annotation { "Feature Type Name" : "Feature", "Feature Type Description" : "" }
export const myFeature = defineFeature(function(context is Context, id is Id, definition is map)
    precondition{}
    {
        {
            var Q0;
            Q0=qCreatedBy(makeId("Top.planeOp"),FACE);
            var sketch = newSketch(context, id + "F0", { "sketchPlane" : qUnion([Q0])});
            skLineSegment(sketch, "E0.bottom", {"start": v(-2.5, 54.86) * mm, "end": v(-0.5, 54.86) * mm});
            skLineSegment(sketch, "E0.right", {"start": v(-0.5, 54.86) * mm, "end": v(-0.5, 51.86) * mm});
            skLineSegment(sketch, "E1", {"start": v(-5.5, 18.86) * mm, "end": v(-2.5, 54.86) * mm});
            skLineSegment(sketch, "E2", {"start": v(-5.5, 18.86) * mm, "end": v(-26.33, -16.13) * mm});
            skLineSegment(sketch, "E3", {"start": v(-0.5, 18.86) * mm, "end": v(-2.64, 6.75) * mm});
            skLineSegment(sketch, "E4", {"start": v(-12.15, -20.66) * mm, "end": v(-23.75, -20.66) * mm});
            skPoint(sketch, "E5.visualSharp", {"position": v(-29.03, -20.66) * mm});
            skArc(sketch, "E5.filletArc", {"start": v(-26.33, -16.13) * mm, "mid": v(-26.36, -19.15) * mm, "end": v(-23.75, -20.66) * mm});
            skPoint(sketch, "E6.visualSharp", {"position": v(-7.47, -20.66) * mm});
            skLineSegment(sketch, "E7", {"start": v(-6.12, -13.03) * mm, "end": v(-7.03, -18.18) * mm});
            skLineSegment(sketch, "E8", {"start": v(-9.99, -20.66) * mm, "end": v(-12.15, -20.66) * mm});
            skArc(sketch, "E9.filletArc", {"start": v(-9.99, -20.66) * mm, "mid": v(-8.06, -19.96) * mm, "end": v(-7.03, -18.18) * mm});
            skLineSegment(sketch, "E10.0", {"start": v(-6.02, 13.1) * mm, "end": v(-24.63, -18.16) * mm});
            skLineSegment(sketch, "E10.1", {"start": v(-12.15, -18.16) * mm, "end": v(-24.63, -18.16) * mm});
            skLineSegment(sketch, "E10.2", {"start": v(-4.17, 12.42) * mm, "end": v(-8.59, -12.6) * mm});
            skLineSegment(sketch, "E10.3", {"start": v(-8.59, -12.6) * mm, "end": v(-9.57, -18.16) * mm});
            skLineSegment(sketch, "E10.4", {"start": v(-9.57, -18.16) * mm, "end": v(-12.15, -18.16) * mm});
            skPoint(sketch, "E11.visualSharp", {"position": v(-3.23, 17.8) * mm});
            skArc(sketch, "E11.filletArc", {"start": v(-4.17, 12.42) * mm, "mid": v(-4.81, 13.53) * mm, "end": v(-6.02, 13.1) * mm});
            skArc(sketch, "E12", {"start": v(-1.44, 8.44) * mm, "mid": v(-2.1, 7.64) * mm, "end": v(-2.64, 6.75) * mm});
            skArc(sketch, "E13", {"start": v(-1.18, 6.39) * mm, "mid": v(-2.23, 5.44) * mm, "end": v(-3.07, 4.29) * mm});
            skLineSegment(sketch, "E14.trimOffspring", {"start": v(-3.07, 4.29) * mm, "end": v(-6.12, -13.03) * mm});
            skArc(sketch, "E15.MirrorCS", {"start": v(9.99, -20.66) * mm, "mid": v(8.06, -19.96) * mm, "end": v(7.03, -18.18) * mm});
            skLineSegment(sketch, "E16.MirrorCS", {"start": v(9.99, -20.66) * mm, "end": v(12.15, -20.66) * mm});
            skLineSegment(sketch, "E17.MirrorCS", {"start": v(9.57, -18.16) * mm, "end": v(12.15, -18.16) * mm});
            skArc(sketch, "E18.MirrorCS", {"start": v(4.17, 12.42) * mm, "mid": v(4.81, 13.53) * mm, "end": v(6.02, 13.1) * mm});
            skArc(sketch, "E19.MirrorCS", {"start": v(26.33, -16.13) * mm, "mid": v(26.36, -19.15) * mm, "end": v(23.75, -20.66) * mm});
            skArc(sketch, "E20.MirrorCS", {"start": v(1.44, 8.44) * mm, "mid": v(2.1, 7.64) * mm, "end": v(2.64, 6.75) * mm});
            skLineSegment(sketch, "E21.MirrorCS", {"start": v(0.5, 18.86) * mm, "end": v(2.64, 6.75) * mm});
            skLineSegment(sketch, "E22.MirrorCS", {"start": v(6.12, -13.03) * mm, "end": v(7.03, -18.18) * mm});
            skLineSegment(sketch, "E23.MirrorCS", {"start": v(2.5, 54.86) * mm, "end": v(0.5, 54.86) * mm});
            skArc(sketch, "E24.MirrorCS", {"start": v(1.18, 6.39) * mm, "mid": v(2.23, 5.44) * mm, "end": v(3.07, 4.29) * mm});
            skLineSegment(sketch, "E25.MirrorCS", {"start": v(8.59, -12.6) * mm, "end": v(9.57, -18.16) * mm});
            skLineSegment(sketch, "E26.MirrorCS", {"start": v(0, 9.58) * mm, "end": v(0, 9.05) * mm, "construction": true});
            skLineSegment(sketch, "E27.MirrorCS", {"start": v(12.15, -20.66) * mm, "end": v(23.75, -20.66) * mm});
            skLineSegment(sketch, "E28.MirrorCS", {"start": v(12.15, -18.16) * mm, "end": v(24.63, -18.16) * mm});
            skPoint(sketch, "E29.MirrorP", {"position": v(7.47, -20.66) * mm});
            skLineSegment(sketch, "E30.MirrorCS", {"start": v(0.5, 54.86) * mm, "end": v(0.5, 51.86) * mm});
            skLineSegment(sketch, "E31.MirrorCS", {"start": v(5.5, 18.86) * mm, "end": v(26.33, -16.13) * mm});
            skLineSegment(sketch, "E32.MirrorCS", {"start": v(6.02, 13.1) * mm, "end": v(24.63, -18.16) * mm});
            skLineSegment(sketch, "E33.MirrorCS", {"start": v(3.07, 4.29) * mm, "end": v(6.12, -13.03) * mm});
            skLineSegment(sketch, "E34.MirrorCS", {"start": v(4.17, 12.42) * mm, "end": v(8.59, -12.6) * mm});
            skPoint(sketch, "E35.MirrorP", {"position": v(3.23, 17.8) * mm});
            skPoint(sketch, "E36.MirrorP", {"position": v(29.03, -20.66) * mm});
            skLineSegment(sketch, "E37.MirrorCS", {"start": v(5.5, 18.86) * mm, "end": v(2.5, 54.86) * mm});
            skPoint(sketch, "E38.visualSharp", {"position": v(0, 9.58) * mm});
            skArc(sketch, "E38.filletArc", {"start": v(1.44, 8.44) * mm, "mid": v(0, 9.05) * mm, "end": v(-1.44, 8.44) * mm});
            skPoint(sketch, "E39.visualSharp", {"position": v(0, 7.08) * mm});
            skArc(sketch, "E39.filletArc", {"start": v(1.18, 6.39) * mm, "mid": v(0, 6.77) * mm, "end": v(-1.18, 6.39) * mm});
            skLineSegment(sketch, "E40", {"start": v(-0.5, 51.86) * mm, "end": v(-1.25, 51.86) * mm});
            skLineSegment(sketch, "E41", {"start": v(-1.25, 51.86) * mm, "end": v(-1.25, 18.86) * mm});
            skLineSegment(sketch, "E42", {"start": v(-1.25, 18.86) * mm, "end": v(-0.5, 18.86) * mm});
            skLineSegment(sketch, "E43.MirrorCS", {"start": v(1.25, 51.86) * mm, "end": v(1.25, 18.86) * mm});
            skLineSegment(sketch, "E44.MirrorCS", {"start": v(0.5, 51.86) * mm, "end": v(1.25, 51.86) * mm});
            skLineSegment(sketch, "E45.MirrorCS", {"start": v(1.25, 18.86) * mm, "end": v(0.5, 18.86) * mm});
            skPoint(sketch, "E46.orphan", {"position": v(0, 89.9) * mm});
            skLineSegment(sketch, "E47.trimOffspring", {"start": v(0, 7.08) * mm, "end": v(0, 6.77) * mm, "construction": true});
            skSolve(sketch);
        }
        {
            var Q0;
            Q0=makeQuery(id+"F0.imprint","IMPRINT",FACE,{"disambiguationData":[TD([[makeQuery(id+"F0.imprint","IMPRINT",EDGE,{"derivedFrom":sQuery(id+"F0.wireOp",EDGE,"E0.bottom")}),-1.0]])]});
            extrude(context, id + "F1", {"entities" : qUnion([Q0]), "depth" : 6 * mm});
        }
        {
            var Q0;
            Q0=makeQuery(id+"F1.opExtrude","CAP_EDGE",EDGE,{"disambiguationData":[OSD([sQuery(id+"F0.wireOp",EDGE,"E37.MirrorCS")])],"isStart":false});
            var Q1;
            Q1=makeQuery(id+"F1.opExtrude","CAP_EDGE",EDGE,{"disambiguationData":[OSD([sQuery(id+"F0.wireOp",EDGE,"E1")])],"isStart":false});
            var Q2;
            Q2=makeQuery(id+"F1.opExtrude","CAP_EDGE",EDGE,{"disambiguationData":[OSD([sQuery(id+"F0.wireOp",EDGE,"E2")])],"isStart":false});
            var Q3;
            Q3=makeQuery(id+"F1.opExtrude","CAP_EDGE",EDGE,{"disambiguationData":[OSD([sQuery(id+"F0.wireOp",EDGE,"E4"),sQuery(id+"F0.wireOp",EDGE,"E8")])],"isStart":false});
            var Q4;
            Q4=makeQuery(id+"F1.opExtrude","CAP_EDGE",EDGE,{"disambiguationData":[OSD([sQuery(id+"F0.wireOp",EDGE,"E5.filletArc")])],"isStart":false});
            var Q5;
            Q5=makeQuery(id+"F1.opExtrude","CAP_EDGE",EDGE,{"disambiguationData":[OSD([sQuery(id+"F0.wireOp",EDGE,"E9.filletArc")])],"isStart":false});
            var Q6;
            Q6=makeQuery(id+"F1.opExtrude","CAP_EDGE",EDGE,{"disambiguationData":[OSD([sQuery(id+"F0.wireOp",EDGE,"E15.MirrorCS")])],"isStart":false});
            var Q7;
            Q7=makeQuery(id+"F1.opExtrude","CAP_EDGE",EDGE,{"disambiguationData":[OSD([sQuery(id+"F0.wireOp",EDGE,"E16.MirrorCS"),sQuery(id+"F0.wireOp",EDGE,"E27.MirrorCS")])],"isStart":false});
            var Q8;
            Q8=makeQuery(id+"F1.opExtrude","CAP_EDGE",EDGE,{"disambiguationData":[OSD([sQuery(id+"F0.wireOp",EDGE,"E19.MirrorCS")])],"isStart":false});
            var Q9;
            Q9=makeQuery(id+"F1.opExtrude","CAP_EDGE",EDGE,{"disambiguationData":[OSD([sQuery(id+"F0.wireOp",EDGE,"E31.MirrorCS")])],"isStart":false});
            var Q10;
            Q10=makeQuery(id+"F1.opExtrude","CAP_EDGE",EDGE,{"disambiguationData":[OSD([sQuery(id+"F0.wireOp",EDGE,"E0.bottom")])],"isStart":false});
            var Q11;
            Q11=makeQuery(id+"F1.opExtrude","CAP_EDGE",EDGE,{"disambiguationData":[OSD([sQuery(id+"F0.wireOp",EDGE,"E23.MirrorCS")])],"isStart":false});
            var Q12;
            Q12=makeQuery(id+"F1.opExtrude","CAP_EDGE",EDGE,{"disambiguationData":[OSD([sQuery(id+"F0.wireOp",EDGE,"E7"),sQuery(id+"F0.wireOp",EDGE,"E14.trimOffspring")])],"isStart":false});
            var Q13;
            Q13=makeQuery(id+"F1.opExtrude","CAP_EDGE",EDGE,{"disambiguationData":[OSD([sQuery(id+"F0.wireOp",EDGE,"E24.MirrorCS")])],"isStart":false});
            chamfer(context, id + "F2", {"entities" : qUnion([Q0, Q1, Q2, Q3, Q4, Q5, Q6, Q7, Q8, Q9, Q10, Q11, Q12, Q13]), "width" : 1 * mm, "tangentPropagation" : true});
        }
        {
            var Q0;
            Q0=makeQuery(id+"F1.opExtrude","CAP_EDGE",EDGE,{"disambiguationData":[OSD([sQuery(id+"F0.wireOp",EDGE,"E4"),sQuery(id+"F0.wireOp",EDGE,"E8")])],"isStart":true});
            var Q1;
            Q1=makeQuery(id+"F1.opExtrude","CAP_EDGE",EDGE,{"disambiguationData":[OSD([sQuery(id+"F0.wireOp",EDGE,"E7"),sQuery(id+"F0.wireOp",EDGE,"E14.trimOffspring")])],"isStart":true});
            var Q2;
            Q2=makeQuery(id+"F1.opExtrude","CAP_EDGE",EDGE,{"disambiguationData":[OSD([sQuery(id+"F0.wireOp",EDGE,"E13")])],"isStart":true});
            var Q3;
            Q3=makeQuery(id+"F1.opExtrude","CAP_EDGE",EDGE,{"disambiguationData":[OSD([sQuery(id+"F0.wireOp",EDGE,"E22.MirrorCS"),sQuery(id+"F0.wireOp",EDGE,"E33.MirrorCS")])],"isStart":true});
            var Q4;
            Q4=makeQuery(id+"F1.opExtrude","CAP_EDGE",EDGE,{"disambiguationData":[OSD([sQuery(id+"F0.wireOp",EDGE,"E37.MirrorCS")])],"isStart":true});
            var Q5;
            Q5=makeQuery(id+"F1.opExtrude","CAP_EDGE",EDGE,{"disambiguationData":[OSD([sQuery(id+"F0.wireOp",EDGE,"E1")])],"isStart":true});
            var Q6;
            Q6=makeQuery(id+"F1.opExtrude","CAP_EDGE",EDGE,{"disambiguationData":[OSD([sQuery(id+"F0.wireOp",EDGE,"E0.bottom")])],"isStart":true});
            var Q7;
            Q7=makeQuery(id+"F1.opExtrude","CAP_EDGE",EDGE,{"disambiguationData":[OSD([sQuery(id+"F0.wireOp",EDGE,"E23.MirrorCS")])],"isStart":true});
            var Q8;
            Q8=makeQuery(id+"F1.opExtrude","SWEPT_EDGE",EDGE,{"disambiguationData":[OSD([sQuery(id+"F0.wireOp",EDGE,"E0.bottom"),sQuery(id+"F0.wireOp",EDGE,"E1")])]});
            var Q9;
            Q9=makeQuery(id+"F1.opExtrude","SWEPT_EDGE",EDGE,{"disambiguationData":[OSD([sQuery(id+"F0.wireOp",EDGE,"E23.MirrorCS"),sQuery(id+"F0.wireOp",EDGE,"E37.MirrorCS")])]});
            chamfer(context, id + "F3", {"entities" : qUnion([Q0, Q1, Q2, Q3, Q4, Q5, Q6, Q7, Q8, Q9]), "width" : 1 * mm, "tangentPropagation" : true});
        }
        {
            var Q0;
            Q0=makeQuery(id+"F1.opExtrude","CAP_EDGE",EDGE,{"disambiguationData":[OSD([sQuery(id+"F0.wireOp",EDGE,"E11.filletArc")])],"isStart":true});
            var Q1;
            Q1=makeQuery(id+"F1.opExtrude","CAP_EDGE",EDGE,{"disambiguationData":[OSD([sQuery(id+"F0.wireOp",EDGE,"E10.0")])],"isStart":true});
            var Q2;
            Q2=makeQuery(id+"F1.opExtrude","CAP_EDGE",EDGE,{"disambiguationData":[OSD([sQuery(id+"F0.wireOp",EDGE,"E10.2"),sQuery(id+"F0.wireOp",EDGE,"E10.3")])],"isStart":true});
            var Q3;
            Q3=makeQuery(id+"F1.opExtrude","CAP_EDGE",EDGE,{"disambiguationData":[OSD([sQuery(id+"F0.wireOp",EDGE,"E10.1"),sQuery(id+"F0.wireOp",EDGE,"E10.4")])],"isStart":true});
            var Q4;
            Q4=makeQuery(id+"F1.opExtrude","CAP_EDGE",EDGE,{"disambiguationData":[OSD([sQuery(id+"F0.wireOp",EDGE,"E18.MirrorCS")])],"isStart":true});
            var Q5;
            Q5=makeQuery(id+"F1.opExtrude","CAP_EDGE",EDGE,{"disambiguationData":[OSD([sQuery(id+"F0.wireOp",EDGE,"E32.MirrorCS")])],"isStart":true});
            var Q6;
            Q6=makeQuery(id+"F1.opExtrude","CAP_EDGE",EDGE,{"disambiguationData":[OSD([sQuery(id+"F0.wireOp",EDGE,"E17.MirrorCS"),sQuery(id+"F0.wireOp",EDGE,"E28.MirrorCS")])],"isStart":true});
            var Q7;
            Q7=makeQuery(id+"F1.opExtrude","CAP_EDGE",EDGE,{"disambiguationData":[OSD([sQuery(id+"F0.wireOp",EDGE,"E17.MirrorCS"),sQuery(id+"F0.wireOp",EDGE,"E28.MirrorCS")])],"isStart":false});
            var Q8;
            Q8=makeQuery(id+"F1.opExtrude","CAP_EDGE",EDGE,{"disambiguationData":[OSD([sQuery(id+"F0.wireOp",EDGE,"E10.1"),sQuery(id+"F0.wireOp",EDGE,"E10.4")])],"isStart":false});
            var Q9;
            Q9=makeQuery(id+"F1.opExtrude","CAP_EDGE",EDGE,{"disambiguationData":[OSD([sQuery(id+"F0.wireOp",EDGE,"E25.MirrorCS"),sQuery(id+"F0.wireOp",EDGE,"E34.MirrorCS")])],"isStart":false});
            var Q10;
            Q10=makeQuery(id+"F1.opExtrude","CAP_EDGE",EDGE,{"disambiguationData":[OSD([sQuery(id+"F0.wireOp",EDGE,"E10.2"),sQuery(id+"F0.wireOp",EDGE,"E10.3")])],"isStart":false});
            fillet(context, id + "F4", {"entities" : qUnion([Q0, Q1, Q2, Q3, Q4, Q5, Q6, Q7, Q8, Q9, Q10]), "radius" : 2 * mm, "tangentPropagation" : true, "allowEdgeOverflow" : false});
        }
        {
            var Q0;
            Q0=makeQuery(id+"F1.opExtrude","SWEPT_FACE",FACE,{"disambiguationData":[OSD([sQuery(id+"F0.wireOp",EDGE,"E37.MirrorCS")])]});
            var sketch = newSketch(context, id + "F5", { "sketchPlane" : qUnion([Q0])});
            skText(sketch, "E48", { "text": "BAG CLIP", "fontName": "OpenSans-Bold.ttf"});
            skLineSegment(sketch, "E49", {"start": v(43.5, 3) * mm, "end": v(53.55, 3) * mm, "construction": true});
            const initialGuessF5  = {"E48": [0.01834, 0.001, 1, 0, 0.004]};
            skSetInitialGuess(sketch, initialGuessF5);
            skSolve(sketch);
        }
        {
            var Q0;
            Q0=qSketchRegion(id+"F5",true);
            extrude(context, id + "F6", {"entities" : qUnion([Q0]), "operationType" : NewBodyOperationType.REMOVE, "oppositeDirection" : true, "depth" : 1 * mm});
        }
        {
            var Q0;
            Q0=makeQuery(id+"F1.opExtrude","SWEPT_EDGE",EDGE,{"disambiguationData":[OSD([sQuery(id+"F0.wireOp",EDGE,"E3"),sQuery(id+"F0.wireOp",EDGE,"E12")])]});
            var Q1;
            Q1=makeQuery(id+"F1.opExtrude","SWEPT_EDGE",EDGE,{"disambiguationData":[OSD([sQuery(id+"F0.wireOp",EDGE,"E20.MirrorCS"),sQuery(id+"F0.wireOp",EDGE,"E21.MirrorCS")])]});
            var Q2;
            Q2=makeQuery(id+"F1.opExtrude","SWEPT_EDGE",EDGE,{"disambiguationData":[OSD([sQuery(id+"F0.wireOp",EDGE,"E24.MirrorCS"),sQuery(id+"F0.wireOp",EDGE,"E33.MirrorCS")])]});
            var Q3;
            Q3=makeQuery(id+"F1.opExtrude","SWEPT_EDGE",EDGE,{"disambiguationData":[OSD([sQuery(id+"F0.wireOp",EDGE,"E13"),sQuery(id+"F0.wireOp",EDGE,"E14.trimOffspring")])]});
            fillet(context, id + "F7", {"entities" : qUnion([Q0, Q1, Q2, Q3]), "radius" : 1 * mm, "tangentPropagation" : true, "allowEdgeOverflow" : false});
        }
        {
            var Q0;
            Q0=makeQuery(id+"F1.opExtrude","SWEPT_EDGE",EDGE,{"disambiguationData":[OSD([sQuery(id+"F0.wireOp",EDGE,"E21.MirrorCS"),sQuery(id+"F0.wireOp",EDGE,"E45.MirrorCS")])]});
            var Q1;
            Q1=makeQuery(id+"F1.opExtrude","SWEPT_EDGE",EDGE,{"disambiguationData":[OSD([sQuery(id+"F0.wireOp",EDGE,"E3"),sQuery(id+"F0.wireOp",EDGE,"E42")])]});
            chamfer(context, id + "F8", {"entities" : qUnion([Q0, Q1]), "width" : 1 * mm, "tangentPropagation" : true});
        }
        {
            var Q0;
            Q0=qCreatedBy(makeId("Top.planeOp"),FACE);
            var sketch = newSketch(context, id + "F9", { "sketchPlane" : qUnion([Q0])});
            skArc(sketch, "E50", {"start": v(-23.75, -20.66) * mm, "mid": v(0, -33.02) * mm, "end": v(23.75, -20.66) * mm});
            skArc(sketch, "E51", {"start": v(-21.75, -20.66) * mm, "mid": v(0, -30.48) * mm, "end": v(21.75, -20.66) * mm});
            skLineSegment(sketch, "E52", {"start": v(21.75, -20.66) * mm, "end": v(23.75, -20.66) * mm, "construction": true});
            skLineSegment(sketch, "E53", {"start": v(-23.75, -20.66) * mm, "end": v(-21.75, -20.66) * mm, "construction": true});
            skLineSegment(sketch, "E54", {"start": v(-23.75, -20.66) * mm, "end": v(-21.75, -20.66) * mm});
            skLineSegment(sketch, "E55", {"start": v(21.75, -20.66) * mm, "end": v(23.75, -20.66) * mm});
            skSolve(sketch);
        }
        {
            var Q0;
            Q0=makeQuery(id+"F9.imprint","IMPRINT",FACE,{"disambiguationData":[TD([[makeQuery(id+"F9.imprint","IMPRINT",EDGE,{"derivedFrom":sQuery(id+"F9.wireOp",EDGE,"E50")}),1.0]])]});
            extrude(context, id + "F10", {"entities" : qUnion([Q0]), "operationType" : NewBodyOperationType.ADD, "depth" : 6 * mm});
        }
        {
            var Q0;
            Q0=makeQuery(id+"F10.opExtrude","CAP_EDGE",EDGE,{"disambiguationData":[OSD([sQuery(id+"F9.wireOp",EDGE,"E55")])],"isStart":false});
            var Q1;
            Q1=makeQuery(id+"F10.opExtrude","CAP_EDGE",EDGE,{"disambiguationData":[OSD([sQuery(id+"F9.wireOp",EDGE,"E54")])],"isStart":false});
            var Q2;
            Q2=makeQuery(id+"F10.opExtrude","CAP_EDGE",EDGE,{"disambiguationData":[OSD([sQuery(id+"F9.wireOp",EDGE,"E54")])],"isStart":true});
            var Q3;
            Q3=makeQuery(id+"F10.opExtrude","CAP_EDGE",EDGE,{"disambiguationData":[OSD([sQuery(id+"F9.wireOp",EDGE,"E55")])],"isStart":true});
            chamfer(context, id + "F11", {"entities" : qUnion([Q0, Q1, Q2, Q3]), "width" : 1 * mm, "tangentPropagation" : true});
        }
        {
            var Q0;
            {var subQ0=sQuery(id+"F9.wireOp",EDGE,"E51");Q0=makeQuery(id+"F10.boolean.opBoolean","SPLIT",EDGE,{"disambiguationData":[topologyDisambiguationEdgeConnected([makeQuery(id+"F1.opExtrude","SWEPT_FACE",FACE,{"disambiguationData":[OSD([sQuery(id+"F0.wireOp",EDGE,"E16.MirrorCS"),sQuery(id+"F0.wireOp",EDGE,"E27.MirrorCS")])]}),makeQuery(id+"F10.opExtrude","SWEPT_FACE",FACE,{"disambiguationData":[OSD([subQ0])]})])],"derivedFrom":makeQuery(id+"F10.opExtrude","SWEPT_EDGE",EDGE,{"disambiguationData":[OSD([subQ0,sQuery(id+"F9.wireOp",EDGE,"E55")])]})});}
            var Q1;
            {var subQ0=sQuery(id+"F9.wireOp",EDGE,"E51");Q1=makeQuery(id+"F10.boolean.opBoolean","SPLIT",EDGE,{"disambiguationData":[topologyDisambiguationEdgeConnected([makeQuery(id+"F1.opExtrude","SWEPT_FACE",FACE,{"disambiguationData":[OSD([sQuery(id+"F0.wireOp",EDGE,"E4"),sQuery(id+"F0.wireOp",EDGE,"E8")])]}),makeQuery(id+"F10.opExtrude","SWEPT_FACE",FACE,{"disambiguationData":[OSD([subQ0])]})])],"derivedFrom":makeQuery(id+"F10.opExtrude","SWEPT_EDGE",EDGE,{"disambiguationData":[OSD([subQ0,sQuery(id+"F9.wireOp",EDGE,"E54")])]})});}
            var Q2;
            Q2=makeQuery(id+"F10.boolean.opBoolean","MERGE",EDGE,{"derivedFrom":[makeQuery(id+"F1.opExtrude","SWEPT_EDGE",EDGE,{"disambiguationData":[OSD([sQuery(id+"F0.wireOp",EDGE,"E4"),sQuery(id+"F0.wireOp",EDGE,"E5.filletArc")])]}),makeQuery(id+"F10.opExtrude","SWEPT_EDGE",EDGE,{"disambiguationData":[OSD([sQuery(id+"F9.wireOp",EDGE,"E50"),sQuery(id+"F9.wireOp",EDGE,"E54")])]})]});
            var Q3;
            Q3=makeQuery(id+"F10.boolean.opBoolean","MERGE",EDGE,{"derivedFrom":[makeQuery(id+"F1.opExtrude","SWEPT_EDGE",EDGE,{"disambiguationData":[OSD([sQuery(id+"F0.wireOp",EDGE,"E19.MirrorCS"),sQuery(id+"F0.wireOp",EDGE,"E27.MirrorCS")])]}),makeQuery(id+"F10.opExtrude","SWEPT_EDGE",EDGE,{"disambiguationData":[OSD([sQuery(id+"F9.wireOp",EDGE,"E50"),sQuery(id+"F9.wireOp",EDGE,"E55")])]})]});
            fillet(context, id + "F12", {"entities" : qUnion([Q0, Q1, Q2, Q3]), "radius" : 1 * mm, "tangentPropagation" : true, "allowEdgeOverflow" : false});
        }
        {
            var Q0;
            Q0=makeQuery(id+"F10.opExtrude","CAP_EDGE",EDGE,{"disambiguationData":[OSD([sQuery(id+"F9.wireOp",EDGE,"E51")])],"isStart":false});
            var Q1;
            Q1=makeQuery(id+"F10.opExtrude","CAP_EDGE",EDGE,{"disambiguationData":[OSD([sQuery(id+"F9.wireOp",EDGE,"E51")])],"isStart":true});
            fillet(context, id + "F13", {"entities" : qUnion([Q0, Q1]), "radius" : 1 * mm, "tangentPropagation" : true, "allowEdgeOverflow" : false});
        }
        {
            var Q0;
            Q0=makeQuery(id+"F10.opExtrude","CAP_EDGE",EDGE,{"disambiguationData":[OSD([sQuery(id+"F9.wireOp",EDGE,"E50")])],"isStart":true});
            var Q1;
            Q1=makeQuery(id+"F10.opExtrude","CAP_EDGE",EDGE,{"disambiguationData":[OSD([sQuery(id+"F9.wireOp",EDGE,"E50")])],"isStart":false});
            fillet(context, id + "F14", {"entities" : qUnion([Q0, Q1]), "radius" : .5 * mm, "tangentPropagation" : true, "allowEdgeOverflow" : false});
        }
    });